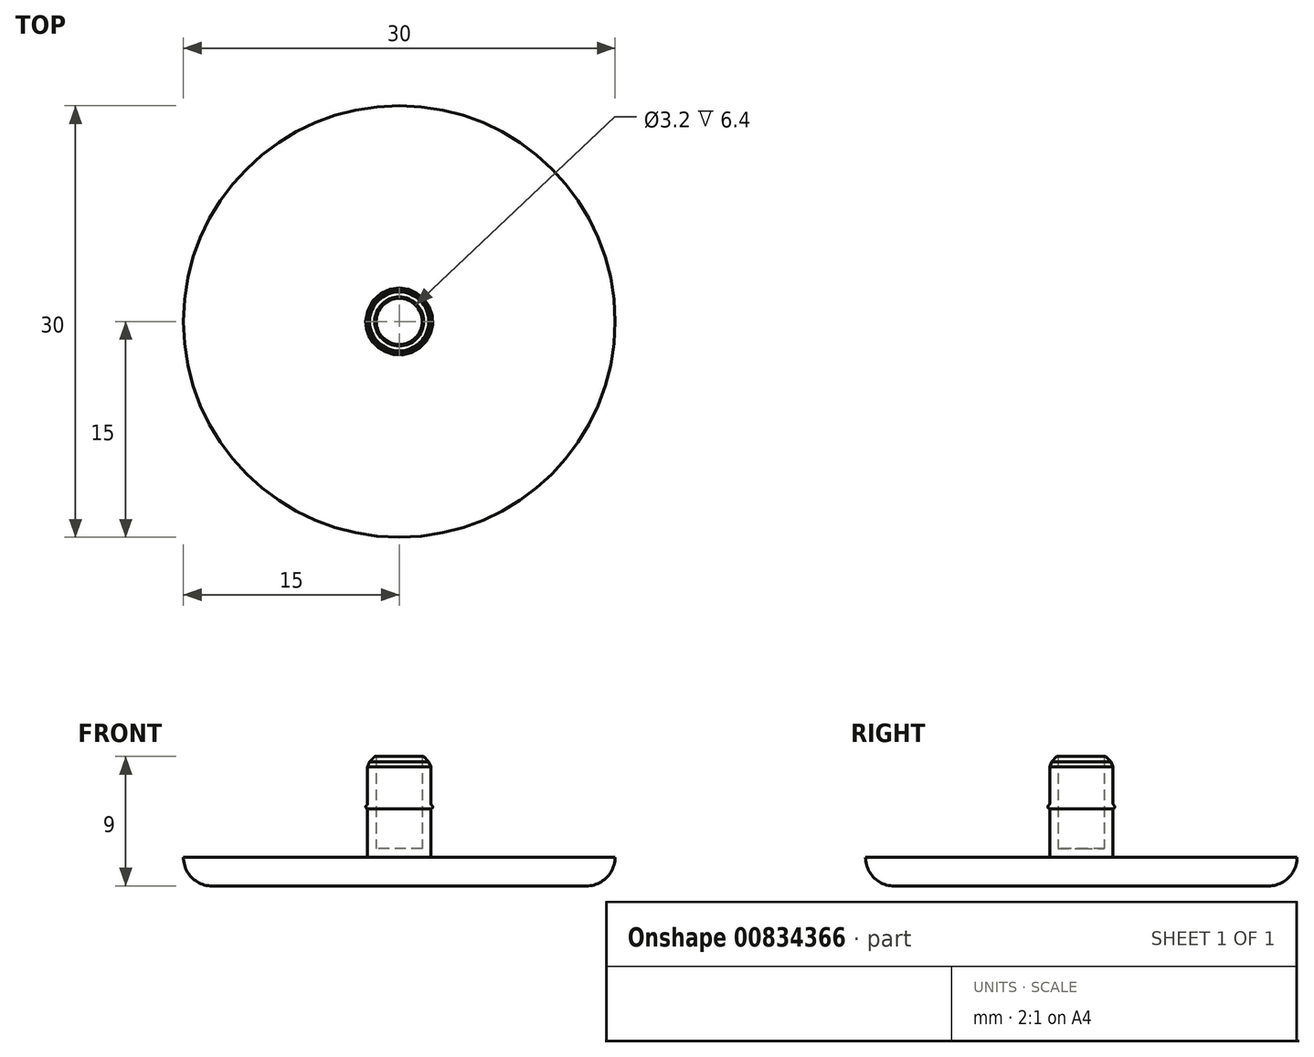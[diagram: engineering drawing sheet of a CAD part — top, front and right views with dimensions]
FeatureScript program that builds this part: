
annotation { "Feature Type Name" : "Feature", "Feature Type Description" : "" }
export const myFeature = defineFeature(function(context is Context, id is Id, definition is map)
    precondition{}
    {
        {
            var Q0;
            Q0=qCreatedBy(makeId("Top.planeOp"),FACE);
            var sketch = newSketch(context, id + "F0", { "sketchPlane" : qUnion([Q0])});
            skCircle(sketch, "E0", {"center": v(0, 0) * mm, "radius": 2.2 * mm});
            skCircle(sketch, "E1", {"center": v(0, 0) * mm, "radius": 15 * mm});
            skSolve(sketch);
        }
        {
            var Q0;
            Q0=makeQuery(id+"F0.imprint","IMPRINT",FACE,{"disambiguationData":[TD([[makeQuery(id+"F0.imprint","IMPRINT",EDGE,{"derivedFrom":sQuery(id+"F0.wireOp",EDGE,"E0")}),1.0]])]});
            extrude(context, id + "F1", {"entities" : qUnion([Q0]), "depth" : 7 * mm, "offsetDistance" : 25 * mm});
        }
        {
            var Q0;
            Q0=makeQuery(id+"F1.opExtrude","CAP_FACE",FACE,{"disambiguationData":[OSD([sQuery(id+"F0.wireOp",EDGE,"E0")])],"isStart":false});
            shell(context, id + "F2", {"entities" : qUnion([Q0]), "thickness" : 0.6 * mm});
        }
        {
            var Q0;
            Q0=makeQuery(id+"F0.imprint","IMPRINT",FACE,{"disambiguationData":[TD([[makeQuery(id+"F0.imprint","IMPRINT",EDGE,{"derivedFrom":sQuery(id+"F0.wireOp",EDGE,"E0")}),-1.0]])]});
            var Q1;
            Q1=makeQuery(id+"F0.imprint","IMPRINT",FACE,{"disambiguationData":[TD([[makeQuery(id+"F0.imprint","IMPRINT",EDGE,{"derivedFrom":sQuery(id+"F0.wireOp",EDGE,"E0")}),1.0]])]});
            extrude(context, id + "F3", {"entities" : qUnion([Q0, Q1]), "operationType" : NewBodyOperationType.ADD, "oppositeDirection" : true, "depth" : 2 * mm, "offsetDistance" : 25 * mm});
        }
        {
            var Q0;
            Q0=makeQuery(id+"F3.opExtrude","CAP_EDGE",EDGE,{"disambiguationData":[OSD([sQuery(id+"F0.wireOp",EDGE,"E1")])],"isStart":false});
            fillet(context, id + "F4", {"entities" : qUnion([Q0]), "radius" : 2 * mm, "tangentPropagation" : true, "allowEdgeOverflow" : false});
        }
        {
            var Q0;
            Q0=qCreatedBy(makeId("Front.planeOp"),FACE);
            var sketch = newSketch(context, id + "F5", { "sketchPlane" : qUnion([Q0])});
            skLineSegment(sketch, "E2.bottom", {"start": v(0, 0) * mm, "end": v(2.2, 0) * mm});
            skLineSegment(sketch, "E2.top", {"start": v(0, 3.5) * mm, "end": v(2.2, 3.5) * mm});
            skLineSegment(sketch, "E2.left", {"start": v(0, 0) * mm, "end": v(0, 3.5) * mm});
            skLineSegment(sketch, "E2.right", {"start": v(2.2, 0) * mm, "end": v(2.2, 3.5) * mm});
            skCircle(sketch, "E3", {"center": v(2.2, 3.5) * mm, "radius": 0.12 * mm});
            skSolve(sketch);
        }
        {
            var Q0;
            {var subQ0=sQuery(id+"F5.wireOp",EDGE,"E2.right");var subQ1=sQuery(id+"F5.wireOp",EDGE,"E2.top");var subQ2=makeQuery(id+"F5.imprint","INTERSECT",VERTEX,{"derivedFrom":[subQ1,subQ0]});Q0=makeQuery(id+"F5.imprint","IMPRINT",FACE,{"disambiguationData":[TD([[makeQuery(id+"F5.imprint","IMPRINT",EDGE,{"disambiguationData":[TD([[subQ2,1.0]])],"derivedFrom":subQ1}),-1.0]])]});}
            var Q1;
            {var subQ0=sQuery(id+"F5.wireOp",EDGE,"E2.right");var subQ1=sQuery(id+"F5.wireOp",EDGE,"E2.top");var subQ2=makeQuery(id+"F5.imprint","INTERSECT",VERTEX,{"derivedFrom":[subQ1,subQ0]});Q1=makeQuery(id+"F5.imprint","IMPRINT",FACE,{"disambiguationData":[TD([[makeQuery(id+"F5.imprint","IMPRINT",EDGE,{"disambiguationData":[TD([[subQ2,1.0]])],"derivedFrom":subQ1}),1.0]])]});}
            var Q2;
            Q2=sQuery(id+"F5.wireOp",EDGE,"E2.left");
            revolve(context, id + "F6", {"operationType" : NewBodyOperationType.ADD, "surfaceOperationType" : NewSurfaceOperationType.NEW, "entities" : qUnion([Q0, Q1]), "axis" : qUnion([Q2]), "revolveType" : RevolveType.TWO_DIRECTIONS, "angle" : 180 * degree, "angleBack" : 180 * degree});
        }
        {
            var Q0;
            Q0=makeQuery(id+"F1.opExtrude","CAP_EDGE",EDGE,{"disambiguationData":[OSD([sQuery(id+"F0.wireOp",EDGE,"E0")])],"isStart":false});
            chamfer(context, id + "F7", {"entities" : qUnion([Q0]), "width" : 0.5 * mm, "tangentPropagation" : true});
        }
        {
            var Q0;
            {var subQ0=sQuery(id+"F0.wireOp",EDGE,"E0");Q0=makeQuery(id+"F7.opChamfer","BLEND_EDGE",EDGE,{"blendedFrom":[makeQuery(id+"F1.opExtrude","CAP_EDGE",EDGE,{"disambiguationData":[OSD([subQ0])],"isStart":false}),makeQuery(id+"F6.boolean.opBoolean","SPLIT",FACE,{"disambiguationData":[TD([makeQuery(id+"F1.opExtrude","CAP_FACE",FACE,{"disambiguationData":[OSD([subQ0])],"isStart":false})])],"derivedFrom":makeQuery(id+"F1.opExtrude","SWEPT_FACE",FACE,{"disambiguationData":[OSD([subQ0])]})})],"blendedInto":[makeQuery(id+"F6.boolean.opBoolean","SPLIT",FACE,{"disambiguationData":[TD([makeQuery(id+"F1.opExtrude","CAP_FACE",FACE,{"disambiguationData":[OSD([subQ0])],"isStart":false})])],"derivedFrom":makeQuery(id+"F1.opExtrude","SWEPT_FACE",FACE,{"disambiguationData":[OSD([subQ0])]})})]});}
            chamfer(context, id + "F8", {"entities" : qUnion([Q0]), "width" : 0.5 * mm, "tangentPropagation" : true});
        }
        {
            var Q0;
            Q0=makeQuery(id+"F6.boolean.opBoolean","INTERSECT",EDGE,{"disambiguationData":[OD(0.0)],"derivedFrom":[makeQuery(id+"F1.opExtrude","SWEPT_FACE",FACE,{"disambiguationData":[OSD([sQuery(id+"F0.wireOp",EDGE,"E0")])]}),makeQuery(id+"F6.opRevolve","SWEPT_FACE",FACE,{"disambiguationData":[OSD([sQuery(id+"F5.wireOp",EDGE,"E3")])]})]});
            fillet(context, id + "F9", {"entities" : qUnion([Q0]), "radius" : 0.2 * mm, "tangentPropagation" : true, "allowEdgeOverflow" : false});
        }
    });
